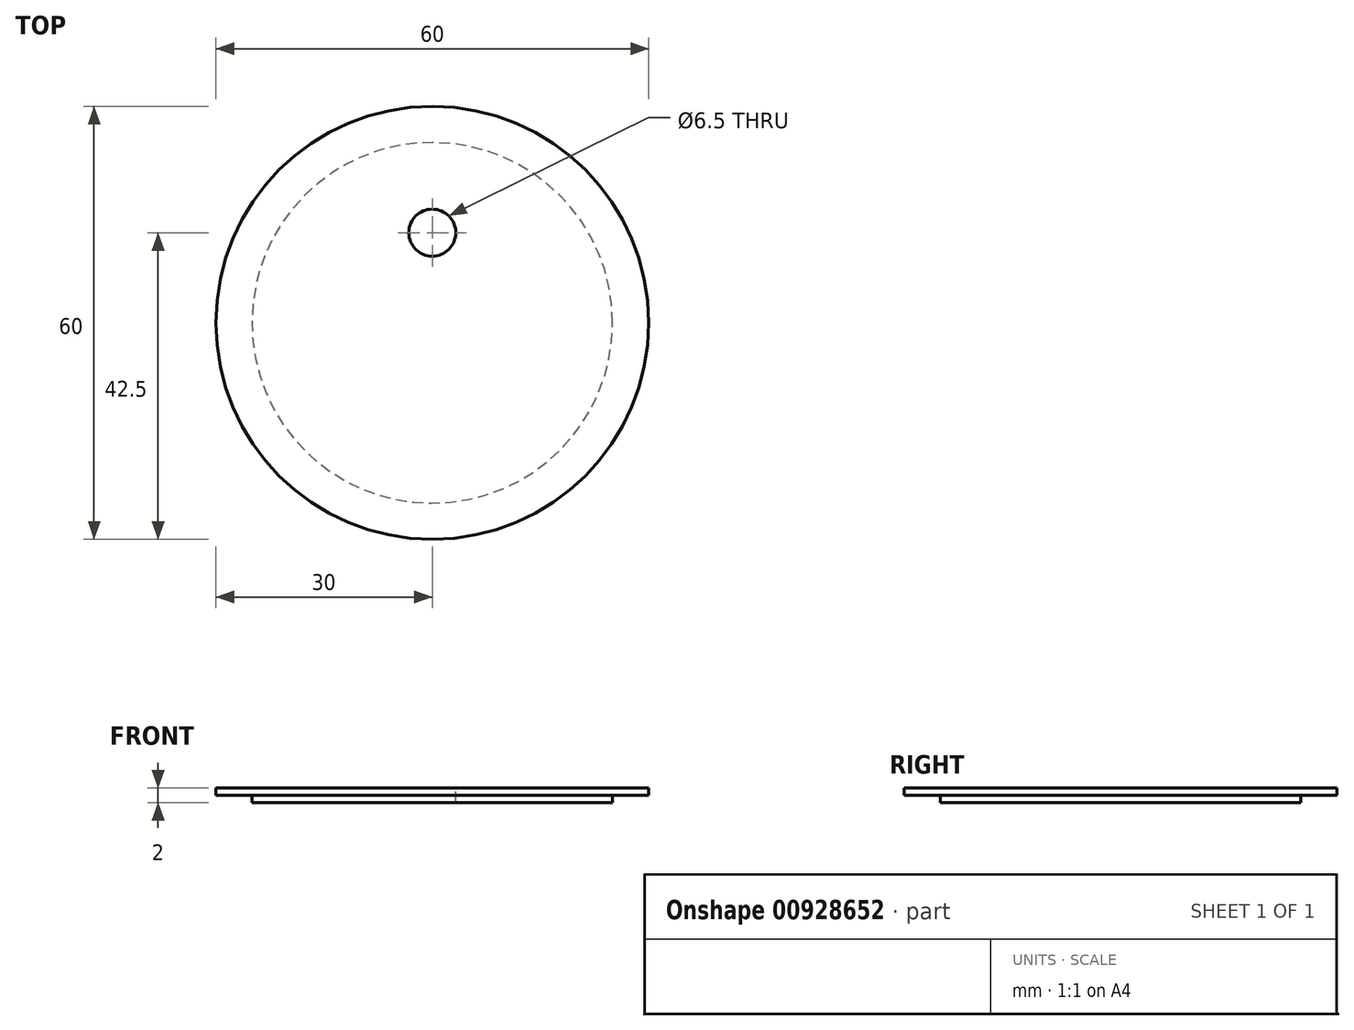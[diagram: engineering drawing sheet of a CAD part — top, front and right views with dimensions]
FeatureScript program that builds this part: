
annotation { "Feature Type Name" : "Feature", "Feature Type Description" : "" }
export const myFeature = defineFeature(function(context is Context, id is Id, definition is map)
    precondition{}
    {
        {
            var Q0;
            Q0=qCreatedBy(makeId("Front.planeOp"),FACE);
            var sketch = newSketch(context, id + "F0", { "sketchPlane" : qUnion([Q0])});
            skLineSegment(sketch, "E0", {"start": v(0, -43.9) * mm, "end": v(0, 38.53) * mm, "construction": true});
            skSolve(sketch);
        }
        {
            var Q0;
            Q0=qCreatedBy(makeId("Top.planeOp"),FACE);
            var sketch = newSketch(context, id + "F1", { "sketchPlane" : qUnion([Q0])});
            skCircle(sketch, "E1", {"center": v(0, 0) * mm, "radius": 25 * mm});
            skLineSegment(sketch, "E2", {"start": v(0, 0) * mm, "end": v(0, 25) * mm, "construction": true});
            skCircle(sketch, "E3", {"center": v(0, 12.5) * mm, "radius": 3.25 * mm});
            skCircle(sketch, "E4", {"center": v(0, 0) * mm, "radius": 30 * mm});
            skSolve(sketch);
        }
        {
            var Q0;
            Q0=makeQuery(id+"F1.imprint","IMPRINT",FACE,{"disambiguationData":[TD([[makeQuery(id+"F1.imprint","IMPRINT",EDGE,{"derivedFrom":sQuery(id+"F1.wireOp",EDGE,"E1")}),1.0]])]});
            var Q1;
            Q1=makeQuery(id+"F1.imprint","IMPRINT",FACE,{"disambiguationData":[TD([[makeQuery(id+"F1.imprint","IMPRINT",EDGE,{"derivedFrom":sQuery(id+"F1.wireOp",EDGE,"E3")}),1.0]])]});
            extrude(context, id + "F2", {"entities" : qUnion([Q0, Q1]), "oppositeDirection" : true, "depth" : 2 * mm, "offsetDistance" : 25 * mm});
        }
        {
            var Q0;
            Q0=makeQuery(id+"F1.imprint","IMPRINT",FACE,{"disambiguationData":[TD([[makeQuery(id+"F1.imprint","IMPRINT",EDGE,{"derivedFrom":sQuery(id+"F1.wireOp",EDGE,"E1")}),-1.0]])]});
            extrude(context, id + "F3", {"entities" : qUnion([Q0]), "operationType" : NewBodyOperationType.ADD, "oppositeDirection" : true, "depth" : 1 * mm, "offsetDistance" : 25 * mm});
        }
        {
            var Q0;
            Q0=makeQuery(id+"F1.imprint","IMPRINT",FACE,{"disambiguationData":[TD([[makeQuery(id+"F1.imprint","IMPRINT",EDGE,{"derivedFrom":sQuery(id+"F1.wireOp",EDGE,"E3")}),1.0]])]});
            extrude(context, id + "F4", {"entities" : qUnion([Q0]), "operationType" : NewBodyOperationType.REMOVE, "oppositeDirection" : true, "depth" : 25 * mm, "offsetDistance" : 25 * mm});
        }
    });
